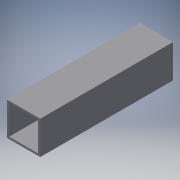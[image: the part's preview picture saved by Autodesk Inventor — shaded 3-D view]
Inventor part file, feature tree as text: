
AUTODESK INVENTOR PART (.ipt)
format: ipt  version: 2016 (Build 200138000, 138)  size: 88,576 bytes
history: native  units: in
note: dims shown in document units (in); Inventor stores cm internally (conversion verified against a paired STEP export)
features: extrude x1, sketch x1
ambient origin geometry x8: Origin, YZ Plane, XZ Plane, XY Plane, X Axis, Y Axis, Z Axis, Center Point
bodies: Solid1 (feature_tree)
feature tree (2):
  extrude  "Extrusion1"  Depth=1.0in
  sketch  "Sketch1"  dims[d0=1.0in d1=1.0in d2=0.0625in d3=3.5in d4=0.0in]
